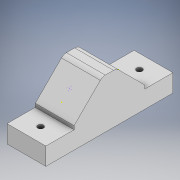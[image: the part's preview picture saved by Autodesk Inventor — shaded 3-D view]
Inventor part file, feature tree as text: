
AUTODESK INVENTOR PART (.ipt)
format: ipt  version: 2022 (Build 260153000, 153)  size: 125,440 bytes
history: native  units: mm
features: sketch x5, extrude x2, hole x1, chamfer x1, fillet x1
ambient origin geometry x8: Origin, YZ Plane, XZ Plane, XY Plane, X Axis, Y Axis, Z Axis, Center Point
bodies: Solid1 (feature_tree)
feature tree (10):
  extrude  "Extrusion1"  Depth=18.0mm TaperAngle=0.0deg
  hole  "Hole1"  [1 undecoded]
  extrude  "Extrusion2"  [1 undecoded]
  chamfer  "Chamfer1"  [1 undecoded]
  fillet  "Fillet1"  [1 undecoded]
  sketch  "Sketch4"
  sketch  "Sketch5"
  sketch  "Sketch1"  dims[d0=10.0mm d1=0.0mm]
  sketch  "Sketch2"  dims[d2=3.242mm d3=8.0mm d4=4.0mm d5=2.0mm d6=90.0deg d7=8.0mm d8=0.0mm d9=18.0mm d10=0.0mm]
  sketch  "Sketch3"  dims[d11=16.0mm d12=2.0mm d13=45.0deg d14=4.0mm]
note: 4 required parameter values undecoded (feature->parameter linkage not recoverable at this tier; creation-order binding heuristic only, values carry confidence <= 0.55)
